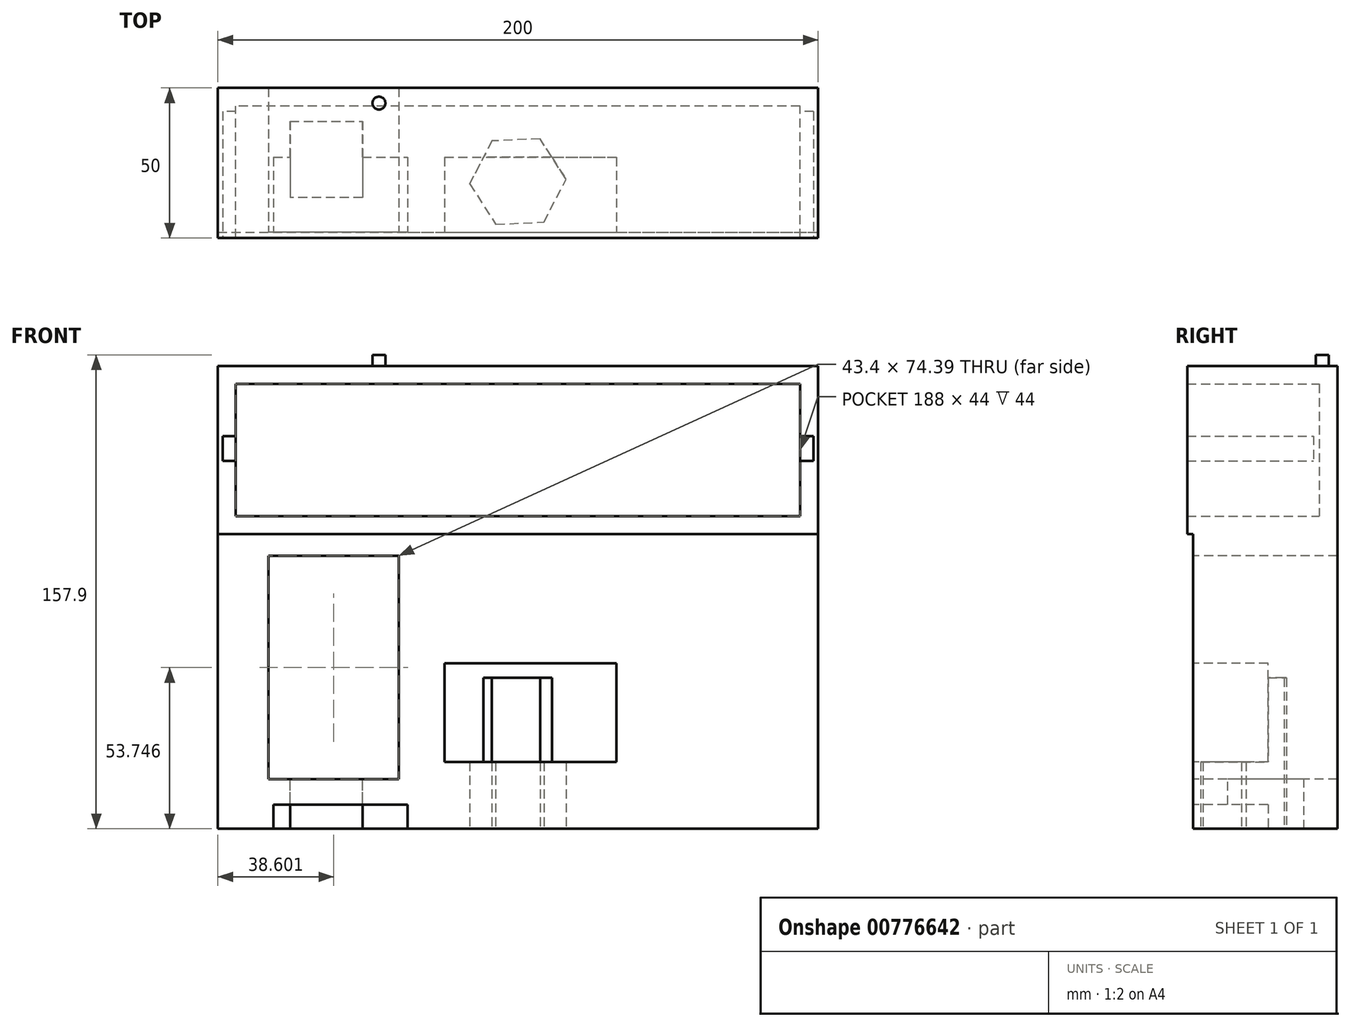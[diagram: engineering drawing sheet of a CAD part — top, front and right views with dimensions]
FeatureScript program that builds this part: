
annotation { "Feature Type Name" : "Feature", "Feature Type Description" : "" }
export const myFeature = defineFeature(function(context is Context, id is Id, definition is map)
    precondition{}
    {
        {
            var Q0;
            Q0=qCreatedBy(makeId("Front.planeOp"),FACE);
            var sketch = newSketch(context, id + "F0", { "sketchPlane" : qUnion([Q0])});
            skLineSegment(sketch, "E0.bottom", {"start": v(100, 28) * mm, "end": v(-100, 28) * mm});
            skLineSegment(sketch, "E0.top", {"start": v(100, -28) * mm, "end": v(-100, -28) * mm});
            skLineSegment(sketch, "E0.left", {"start": v(100, 28) * mm, "end": v(100, -28) * mm});
            skLineSegment(sketch, "E0.right", {"start": v(-100, 28) * mm, "end": v(-100, -28) * mm});
            skPoint(sketch, "E0.middle", {"position": v(0, 0) * mm});
            skSolve(sketch);
        }
        {
            var Q0;
            Q0=makeQuery(id+"F0.imprint","IMPRINT",FACE,{"disambiguationData":[TD([[makeQuery(id+"F0.imprint","IMPRINT",EDGE,{"derivedFrom":sQuery(id+"F0.wireOp",EDGE,"E0.bottom")}),1.0]])]});
            extrude(context, id + "F1", {"entities" : qUnion([Q0]), "depth" : 50 * mm, "offsetDistance" : 25 * mm});
        }
        {
            var Q0;
            Q0=makeQuery(id+"F1.opExtrude","CAP_FACE",FACE,{"disambiguationData":[OSD([sQuery(id+"F0.wireOp",EDGE,"E0.bottom"),sQuery(id+"F0.wireOp",EDGE,"E0.top"),sQuery(id+"F0.wireOp",EDGE,"E0.left"),sQuery(id+"F0.wireOp",EDGE,"E0.right")])],"isStart":false});
            shell(context, id + "F2", {"entities" : qUnion([Q0]), "thickness" : 6 * mm});
        }
        {
            var Q0;
            Q0=qCreatedBy(makeId("Right.planeOp"),FACE);
            var sketch = newSketch(context, id + "F3", { "sketchPlane" : qUnion([Q0])});
            skLineSegment(sketch, "E1.bottom", {"start": v(-7.9, -3.6) * mm, "end": v(-157, -3.6) * mm});
            skLineSegment(sketch, "E1.top", {"start": v(-7.9, 4.7) * mm, "end": v(-157, 4.7) * mm});
            skLineSegment(sketch, "E1.left", {"start": v(-7.9, -3.6) * mm, "end": v(-7.9, 4.7) * mm});
            skLineSegment(sketch, "E1.right", {"start": v(-157, -3.6) * mm, "end": v(-157, 4.7) * mm});
            skSolve(sketch);
        }
        {
            var Q0;
            Q0 = qSketchRegion(id + "F3", true);
            extrude(context, id + "F4", {"entities" : qUnion([Q0]), "operationType" : NewBodyOperationType.REMOVE, "depth" : 98.5 * mm, "offsetDistance" : 25 * mm, "hasSecondDirection" : true, "secondDirectionOppositeDirection" : true, "secondDirectionDepth" : 98.4 * mm});
        }
        {
            var Q0;
            Q0=makeQuery(id+"F1.opExtrude","SWEPT_FACE",FACE,{"disambiguationData":[OSD([sQuery(id+"F0.wireOp",EDGE,"E0.bottom")])]});
            var sketch = newSketch(context, id + "F5", { "sketchPlane" : qUnion([Q0])});
            skCircle(sketch, "E2", {"center": v(-46.3, -5.07) * mm, "radius": 2.15 * mm});
            skSolve(sketch);
        }
        {
            var Q0;
            Q0=makeQuery(id+"F5.imprint","IMPRINT",FACE,{"disambiguationData":[TD([[makeQuery(id+"F5.imprint","IMPRINT",EDGE,{"derivedFrom":sQuery(id+"F5.wireOp",EDGE,"E2")}),1.0]])]});
            var Q1;
            Q1=sQuery(id+"F5.wireOp",EDGE,"E2");
            extrude(context, id + "F6", {"entities" : qUnion([Q0]), "operationType" : NewBodyOperationType.ADD, "surfaceOperationType" : NewSurfaceOperationType.ADD, "surfaceEntities" : qUnion([Q1]), "depth" : 3.7 * mm, "offsetDistance" : 25 * mm});
        }
        {
            var Q0;
            Q0=makeQuery(id+"F1.opExtrude","SWEPT_FACE",FACE,{"disambiguationData":[OSD([sQuery(id+"F0.wireOp",EDGE,"E0.top")])]});
            var sketch = newSketch(context, id + "F7", { "sketchPlane" : qUnion([Q0])});
            skLineSegment(sketch, "E3.bottom", {"start": v(-100, 0) * mm, "end": v(100, 0) * mm});
            skLineSegment(sketch, "E3.top", {"start": v(-100, 48.09) * mm, "end": v(100, 48.09) * mm});
            skLineSegment(sketch, "E3.left", {"start": v(-100, 0) * mm, "end": v(-100, 48.09) * mm});
            skLineSegment(sketch, "E3.right", {"start": v(100, 0) * mm, "end": v(100, 48.09) * mm});
            skSolve(sketch);
        }
        {
            var Q0;
            Q0=makeQuery(id+"F7.imprint","IMPRINT",FACE,{"disambiguationData":[TD([[makeQuery(id+"F7.imprint","IMPRINT",EDGE,{"derivedFrom":sQuery(id+"F7.wireOp",EDGE,"E3.bottom")}),-1.0]])]});
            extrude(context, id + "F8", {"entities" : qUnion([Q0]), "operationType" : NewBodyOperationType.ADD, "depth" : 98.2 * mm, "offsetDistance" : 25 * mm});
        }
        {
            var Q0;
            Q0=makeQuery(id+"F8.opExtrude","SWEPT_FACE",FACE,{"disambiguationData":[OSD([sQuery(id+"F7.wireOp",EDGE,"E3.top")])]});
            var sketch = newSketch(context, id + "F9", { "sketchPlane" : qUnion([Q0])});
            skPoint(sketch, "E4.middle", {"position": v(-57.64, -64.67) * mm});
            skLineSegment(sketch, "E5.bottom", {"start": v(-36.77, -118.1) * mm, "end": v(-81.47, -118.1) * mm});
            skLineSegment(sketch, "E5.top", {"start": v(-36.77, -134.3) * mm, "end": v(-81.47, -134.3) * mm});
            skLineSegment(sketch, "E5.left", {"start": v(-36.77, -118.1) * mm, "end": v(-36.77, -134.3) * mm});
            skLineSegment(sketch, "E5.right", {"start": v(-81.47, -118.1) * mm, "end": v(-81.47, -134.3) * mm});
            skPoint(sketch, "E5.middle", {"position": v(-59.12, -126.2) * mm});
            skSolve(sketch);
        }
        {
            var Q0;
            {var subQ0=sQuery(id+"F9.wireOp",EDGE,"E5.bottom");Q0=makeQuery(id+"F9.imprint","IMPRINT",FACE,{"disambiguationData":[TD([[makeQuery(id+"F9.imprint","IMPRINT",EDGE,{"derivedFrom":subQ0}),1.0]])]});}
            extrude(context, id + "F10", {"entities" : qUnion([Q0]), "operationType" : NewBodyOperationType.REMOVE, "oppositeDirection" : true, "depth" : 25 * mm, "offsetDistance" : 25 * mm});
        }
        {
            var Q0;
            Q0=qCreatedBy(makeId("Front.planeOp"),FACE);
            var sketch = newSketch(context, id + "F11", { "sketchPlane" : qUnion([Q0])});
            skLineSegment(sketch, "E6.bottom", {"start": v(-39.7, -35.26) * mm, "end": v(-83.1, -35.26) * mm});
            skLineSegment(sketch, "E6.top", {"start": v(-39.7, -109.65) * mm, "end": v(-83.1, -109.65) * mm});
            skLineSegment(sketch, "E6.left", {"start": v(-39.7, -35.26) * mm, "end": v(-39.7, -109.65) * mm});
            skLineSegment(sketch, "E6.right", {"start": v(-83.1, -35.26) * mm, "end": v(-83.1, -109.65) * mm});
            skPoint(sketch, "E6.middle", {"position": v(-61.4, -72.45) * mm});
            skSolve(sketch);
        }
        {
            var Q0;
            Q0 = qSketchRegion(id + "F11", true);
            extrude(context, id + "F12", {"entities" : qUnion([Q0]), "operationType" : NewBodyOperationType.REMOVE, "oppositeDirection" : true, "depth" : 55.1 * mm, "offsetDistance" : 25 * mm, "hasSecondDirection" : true, "secondDirectionOppositeDirection" : false, "secondDirectionDepth" : 75 * mm});
        }
        {
            var Q0;
            Q0=makeQuery(id+"F12.boolean.opBoolean","COPY",FACE,{"derivedFrom":makeQuery(id+"F12.opExtrude","SWEPT_FACE",FACE,{"disambiguationData":[OSD([sQuery(id+"F11.wireOp",EDGE,"E6.top")])]})});
            var sketch = newSketch(context, id + "F13", { "sketchPlane" : qUnion([Q0])});
            skLineSegment(sketch, "E7.bottom", {"start": v(-51.79, -11.08) * mm, "end": v(-75.92, -11.08) * mm});
            skLineSegment(sketch, "E7.top", {"start": v(-51.79, -36.5) * mm, "end": v(-75.92, -36.5) * mm});
            skLineSegment(sketch, "E7.left", {"start": v(-51.79, -11.08) * mm, "end": v(-51.79, -36.5) * mm});
            skLineSegment(sketch, "E7.right", {"start": v(-75.92, -11.08) * mm, "end": v(-75.92, -36.5) * mm});
            skPoint(sketch, "E7.middle", {"position": v(-63.85, -23.8) * mm});
            skSolve(sketch);
        }
        {
            var Q0;
            Q0=makeQuery(id+"F13.imprint","IMPRINT",FACE,{"disambiguationData":[TD([[makeQuery(id+"F13.imprint","IMPRINT",EDGE,{"derivedFrom":sQuery(id+"F13.wireOp",EDGE,"E7.bottom")}),1.0]])]});
            extrude(context, id + "F14", {"entities" : qUnion([Q0]), "operationType" : NewBodyOperationType.REMOVE, "oppositeDirection" : true, "depth" : 29.4 * mm, "offsetDistance" : 25 * mm});
        }
        {
            var Q0;
            Q0=makeQuery(id+"F8.opExtrude","CAP_FACE",FACE,{"disambiguationData":[OSD([sQuery(id+"F7.wireOp",EDGE,"E3.bottom"),sQuery(id+"F7.wireOp",EDGE,"E3.top"),sQuery(id+"F7.wireOp",EDGE,"E3.left"),sQuery(id+"F7.wireOp",EDGE,"E3.right")])],"isStart":false});
            var sketch = newSketch(context, id + "F15", { "sketchPlane" : qUnion([Q0])});
            skCircle(sketch, "E8.cCircle", {"center": v(0, 31.2) * mm, "radius": 13.91 * mm, "construction": true});
            skLineSegment(sketch, "E8.0", {"start": v(8.66, 44.73) * mm, "end": v(16.05, 30.46) * mm});
            skLineSegment(sketch, "E8.1", {"start": v(16.05, 30.46) * mm, "end": v(7.39, 16.93) * mm});
            skLineSegment(sketch, "E8.2", {"start": v(7.39, 16.93) * mm, "end": v(-8.66, 17.67) * mm});
            skLineSegment(sketch, "E8.3", {"start": v(-8.66, 17.67) * mm, "end": v(-16.05, 31.93) * mm});
            skLineSegment(sketch, "E8.4", {"start": v(-16.05, 31.93) * mm, "end": v(-7.39, 45.46) * mm});
            skLineSegment(sketch, "E8.5", {"start": v(-7.39, 45.46) * mm, "end": v(8.66, 44.73) * mm});
            skPoint(sketch, "E8.0.midPoint", {"position": v(12.35, 37.6) * mm});
            skSolve(sketch);
        }
        {
            var Q0;
            Q0=makeQuery(id+"F15.imprint","IMPRINT",FACE,{"disambiguationData":[TD([[makeQuery(id+"F15.imprint","IMPRINT",EDGE,{"derivedFrom":sQuery(id+"F15.wireOp",EDGE,"E8.0")}),-1.0]])]});
            extrude(context, id + "F16", {"entities" : qUnion([Q0]), "operationType" : NewBodyOperationType.REMOVE, "oppositeDirection" : true, "depth" : 50.3 * mm, "offsetDistance" : 25 * mm});
        }
        {
            var Q0;
            Q0=makeQuery(id+"F8.opExtrude","SWEPT_FACE",FACE,{"disambiguationData":[OSD([sQuery(id+"F7.wireOp",EDGE,"E3.top")])]});
            var sketch = newSketch(context, id + "F17", { "sketchPlane" : qUnion([Q0])});
            skLineSegment(sketch, "E9.bottom", {"start": v(-24.44, -103.93) * mm, "end": v(32.79, -103.93) * mm});
            skLineSegment(sketch, "E9.top", {"start": v(-24.44, -71.02) * mm, "end": v(32.79, -71.02) * mm});
            skLineSegment(sketch, "E9.left", {"start": v(-24.44, -103.93) * mm, "end": v(-24.44, -71.02) * mm});
            skLineSegment(sketch, "E9.right", {"start": v(32.79, -103.93) * mm, "end": v(32.79, -71.02) * mm});
            skSolve(sketch);
        }
        {
            var Q0;
            Q0=makeQuery(id+"F17.imprint","IMPRINT",FACE,{"disambiguationData":[TD([[makeQuery(id+"F17.imprint","IMPRINT",EDGE,{"derivedFrom":sQuery(id+"F17.wireOp",EDGE,"E9.bottom")}),1.0]])]});
            extrude(context, id + "F18", {"entities" : qUnion([Q0]), "operationType" : NewBodyOperationType.REMOVE, "oppositeDirection" : true, "depth" : 25 * mm, "offsetDistance" : 25 * mm});
        }
    });
